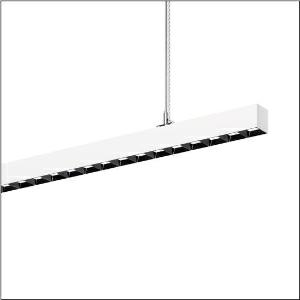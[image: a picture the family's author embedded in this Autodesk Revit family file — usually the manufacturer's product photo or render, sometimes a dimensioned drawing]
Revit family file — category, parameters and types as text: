
# Revit family: silica_r__21_51mx34dc3dwb_cbfc
name_source: partatom
category: Lighting Fixtures
units: mm (PartAtom-declared; Revit-internal decimal feet)

## family parameters
Cut with Voids When Loaded = No
Host = Face
Light Source = No
Part Type = Normal
Room Calculation Point = No
Round Connector Dimension = Use Diameter
Shared = No

## types (1)
- --- (1 x LED, 19200 lm, 129.1 W, 3000K)
    Apparent Load = 129 VA
    CIE Flux Codes = 74 94 99 56 100
    Color Rendering = 80
    Color Temperature = 3000K
    Default Elevation = 1800 mm
    Description = Silica® 21, office luminaire, primary light control with darklight reflector, of PMMA, black, light emission: direct/indirect distribution, primary light characteristic: asymmetric, installation type: suspended mounting, LED, rated luminous flux: 19.200lm, luminous efficacy: 149lm/W, light colour: 830, colour temperature: 3000K, with terminal, 3+2-pole, max. 2.5mm², mains connection: 220..240V, AC, 50/60Hz, rated input power: 129.1W, luminaire housing, of aluminium, traffic white (RAL 9016), length: 3.004mm, width: 53mm, height: 53mm, protection rating (complete): IP20, insulation class (complete): insulation class I (protective earthing), certification: CE, permissible operating ambient temperature: 0..+35°C, standard: EN 50419, packaging unit: 1 piece
    Height = 53 mm
    Lamp = 1 x LED
    Lamp Light Flux = 19200 lm
    Lamp Power = 129.1 W
    Lamp count = 1
    Length = 3004 mm
    Luminous efficacy = 149 lm/W
    Manufacturer = Siteco
    ModVariant = No
    Model = 51MX34DC3DWB
    Mounting Place = Ceiling
    Mounting Type = Pendant
    Number of Poles = 1
    OnlyDefault = Yes
    Power Factor = 1
    Product Name = Silica® 21
    Product group = office luminaire | ceiling pendant
    ProductGroupID = 902
    Protection Class = Protection class I
    Protection Degree = IP 20
    RLX_Detail_Level = 1
    RLX_Emergency_Light_Flux = 0 lm
    RLX_Emergency_Type = 0
    RLX_Emergency_Type_DB = No
    RlxData = <blob elided: 65153 chars, md5=fa68ddd8>
    Socket = socket
    Standby Power = 0 W
    System Light Flux = 19200 lm
    System Power = 129 W
    Type Comments = factory setting: luminous flux: 100 % | dim-lin: 254 | 448 mA
    Type Image = l_1297801.jpg
    URL = http://relux.com
    VarID = @adj_050957
    Voltage = 0 V
    Weight = 0.00 kg
    Width = 53 mm

## geometry (parser evidence)
native form markers: Blend x4, Sweep x13
no freeform markers — native parametric forms only
